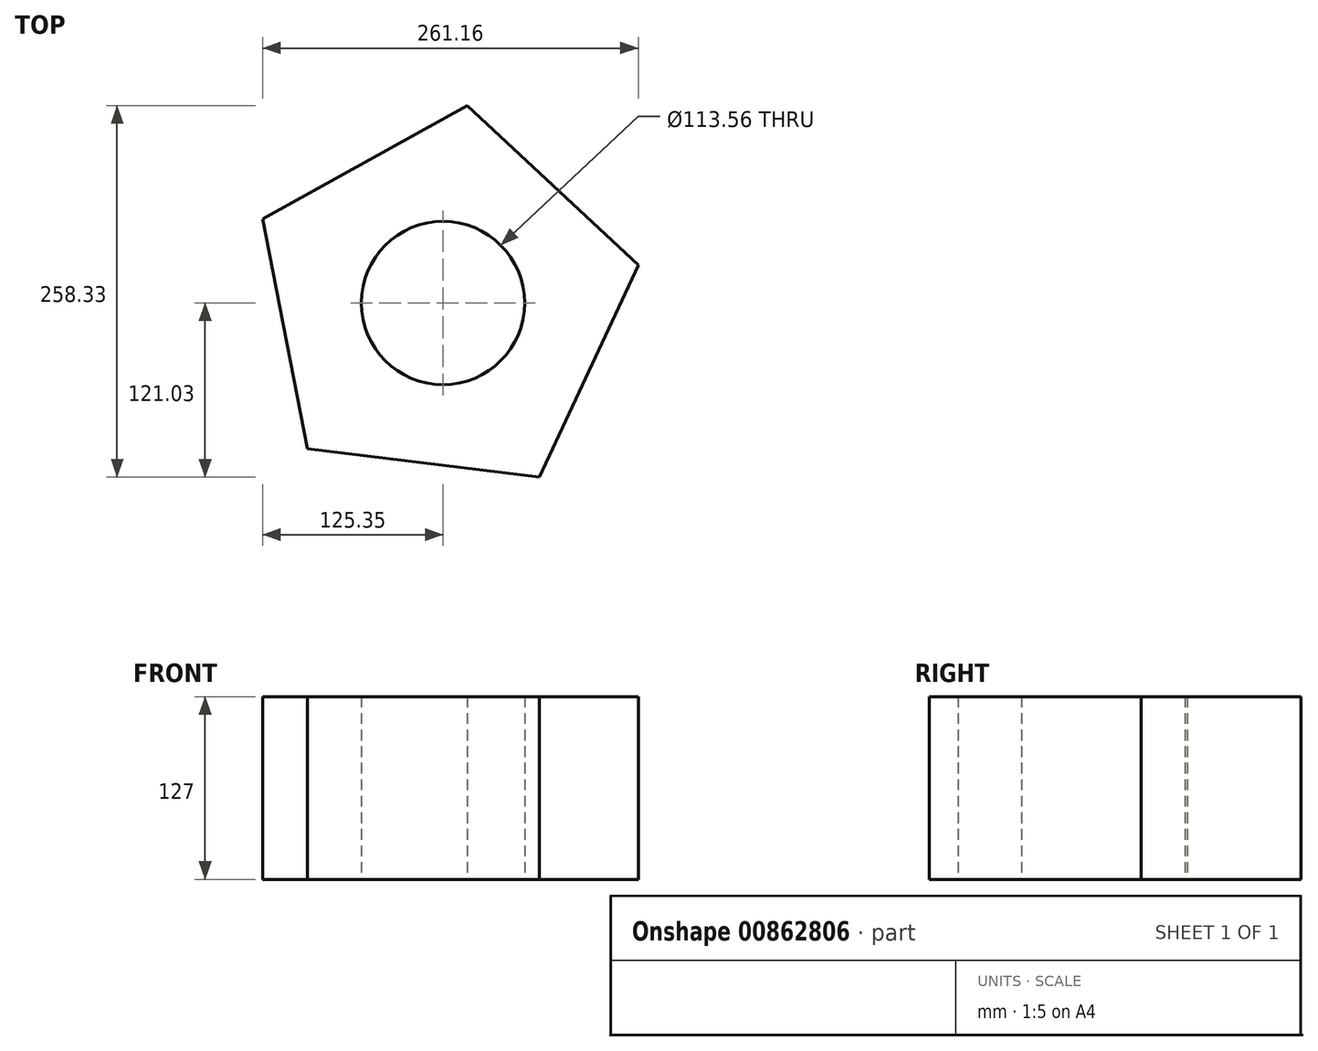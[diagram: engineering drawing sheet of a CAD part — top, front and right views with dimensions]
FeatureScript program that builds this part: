
annotation { "Feature Type Name" : "Feature", "Feature Type Description" : "" }
export const myFeature = defineFeature(function(context is Context, id is Id, definition is map)
    precondition{}
    {
        {
            var Q0;
            Q0=qCreatedBy(makeId("Top.planeOp"),FACE);
            var sketch = newSketch(context, id + "F0", { "sketchPlane" : qUnion([Q0])});
            skCircle(sketch, "E0", {"center": v(0, 0) * mm, "radius": 56.78 * mm});
            skCircle(sketch, "E1.cCircle", {"center": v(0, 0) * mm, "radius": 111.92 * mm, "construction": true});
            skLineSegment(sketch, "E1.0", {"start": v(-125.35, 58.52) * mm, "end": v(16.92, 137.3) * mm});
            skLineSegment(sketch, "E1.1", {"start": v(16.92, 137.3) * mm, "end": v(135.81, 26.33) * mm});
            skLineSegment(sketch, "E1.2", {"start": v(135.81, 26.33) * mm, "end": v(67.01, -121.03) * mm});
            skLineSegment(sketch, "E1.3", {"start": v(67.01, -121.03) * mm, "end": v(-94.4, -101.13) * mm});
            skLineSegment(sketch, "E1.4", {"start": v(-94.4, -101.13) * mm, "end": v(-125.35, 58.52) * mm});
            skPoint(sketch, "E1.0.midPoint", {"position": v(-54.21, 97.91) * mm});
            skSolve(sketch);
        }
        {
            var Q0;
            Q0=makeQuery(id+"F0.imprint","IMPRINT",FACE,{"disambiguationData":[TD([[makeQuery(id+"F0.imprint","IMPRINT",EDGE,{"derivedFrom":sQuery(id+"F0.wireOp",EDGE,"E0")}),-1.0]])]});
            extrude(context, id + "F1", {"entities" : qUnion([Q0]), "depth" : 127 * mm, "offsetDistance" : 25.4 * mm});
        }
    });
